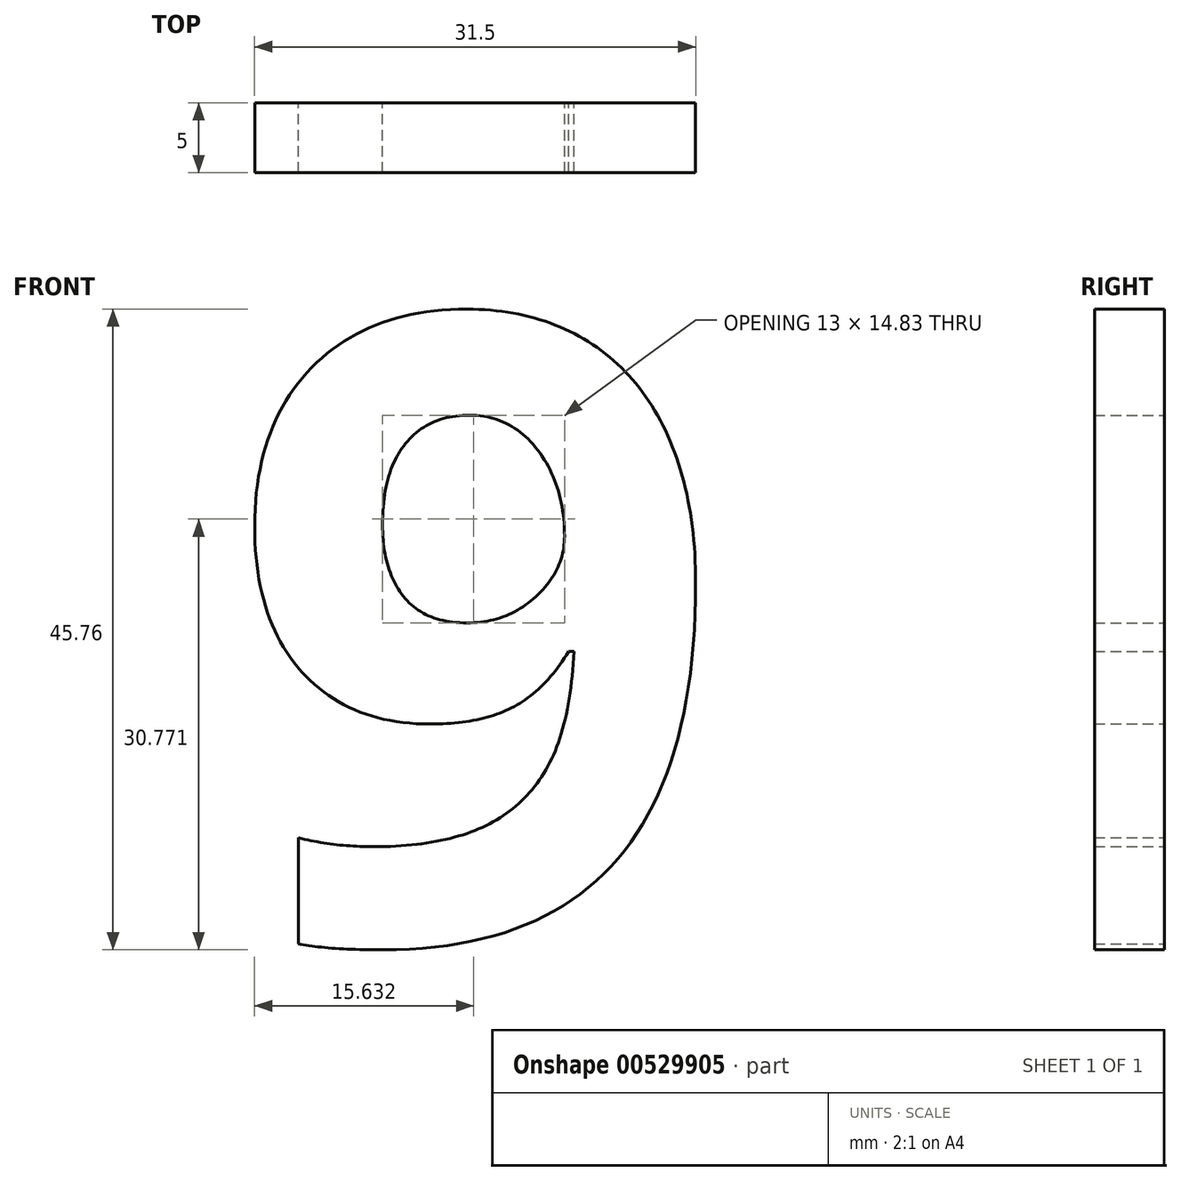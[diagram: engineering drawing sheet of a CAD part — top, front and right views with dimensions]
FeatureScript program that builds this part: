
annotation { "Feature Type Name" : "Feature", "Feature Type Description" : "" }
export const myFeature = defineFeature(function(context is Context, id is Id, definition is map)
    precondition{}
    {
        {
            var Q0;
            Q0=qCreatedBy(makeId("Front.planeOp"),FACE);
            var sketch = newSketch(context, id + "F0", { "sketchPlane" : qUnion([Q0])});
            skText(sketch, "E0", { "text": "9", "fontName": "OpenSans-Bold.ttf"});
            const initialGuessF0  = {"E0": [-0.05739, 0.01298, 1, 0, 0.045]};
            skSetInitialGuess(sketch, initialGuessF0);
            skSolve(sketch);
        }
        {
            var Q0;
            Q0=makeQuery(id+"F0.imprint","IMPRINT",FACE,{"disambiguationData":[TD([[makeQuery(id+"F0.imprint","IMPRINT",EDGE,{"derivedFrom":sQuery(id+"F0.wireOp",EDGE,"E0.sketch_text.stroke-0")}),-1.0]])]});
            extrude(context, id + "F1", {"entities" : qUnion([Q0]), "depth" : 5 * mm, "offsetDistance" : 25 * mm});
        }
    });
